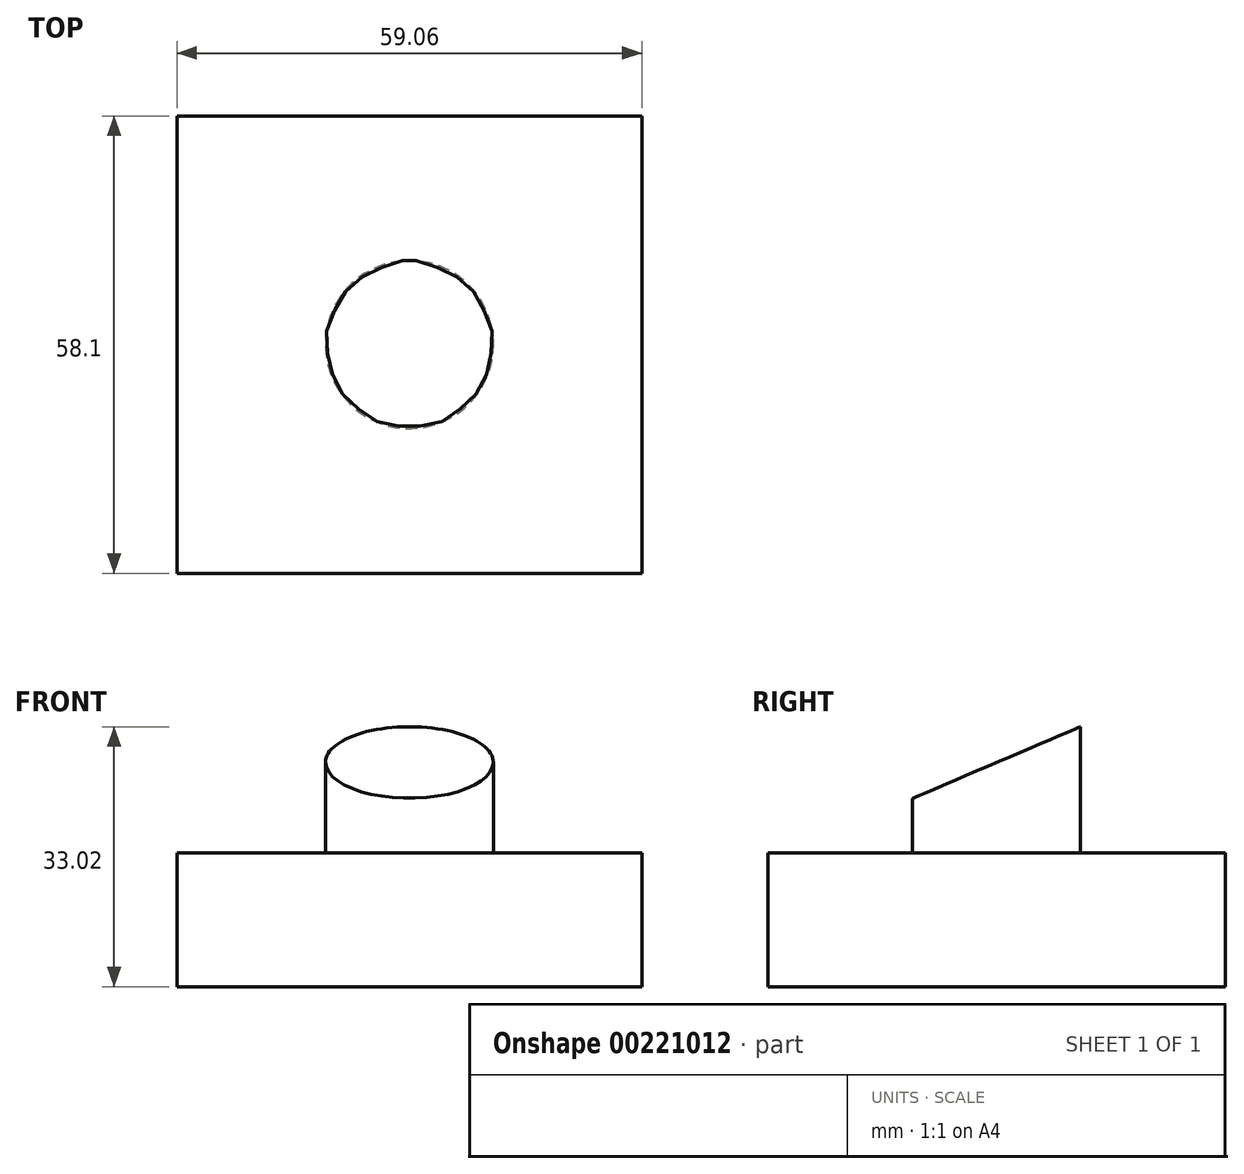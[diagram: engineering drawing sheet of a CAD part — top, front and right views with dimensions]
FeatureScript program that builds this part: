
annotation { "Feature Type Name" : "Feature", "Feature Type Description" : "" }
export const myFeature = defineFeature(function(context is Context, id is Id, definition is map)
    precondition{}
    {
        {
            var Q0;
            Q0=qCreatedBy(makeId("Top.planeOp"),FACE);
            var sketch = newSketch(context, id + "F0", { "sketchPlane" : qUnion([Q0])});
            skLineSegment(sketch, "E0.bottom", {"start": v(-29.53, 29.05) * mm, "end": v(29.53, 29.05) * mm});
            skLineSegment(sketch, "E0.top", {"start": v(-29.53, -29.05) * mm, "end": v(29.53, -29.05) * mm});
            skLineSegment(sketch, "E0.left", {"start": v(-29.53, 29.05) * mm, "end": v(-29.53, -29.05) * mm});
            skLineSegment(sketch, "E0.right", {"start": v(29.53, 29.05) * mm, "end": v(29.53, -29.05) * mm});
            skPoint(sketch, "E0.middle", {"position": v(0, 0) * mm});
            skSolve(sketch);
        }
        {
            var Q0;
            Q0 = qSketchRegion(id + "F0", true);
            extrude(context, id + "F1", {"entities" : qUnion([Q0]), "depth" : 17.02 * mm});
        }
        {
            var Q0;
            Q0=makeQuery(id+"F1.opExtrude","CAP_FACE",FACE,{"disambiguationData":[OSD([sQuery(id+"F0.wireOp",EDGE,"E0.bottom"),sQuery(id+"F0.wireOp",EDGE,"E0.top"),sQuery(id+"F0.wireOp",EDGE,"E0.left"),sQuery(id+"F0.wireOp",EDGE,"E0.right")])],"isStart":false});
            var sketch = newSketch(context, id + "F2", { "sketchPlane" : qUnion([Q0])});
            skCircle(sketch, "E1", {"center": v(0, 0) * mm, "radius": 10.68 * mm});
            skSolve(sketch);
        }
        {
            var Q0;
            Q0 = qSketchRegion(id + "F2", true);
            extrude(context, id + "F3", {"entities" : qUnion([Q0]), "operationType" : NewBodyOperationType.ADD, "depth" : 16 * mm});
        }
        {
            var Q0;
            Q0=qCreatedBy(makeId("Right.planeOp"),FACE);
            var sketch = newSketch(context, id + "F4", { "sketchPlane" : qUnion([Q0])});
            skLineSegment(sketch, "E2", {"start": v(10.68, 33.04) * mm, "end": v(-10.7, 23.9) * mm});
            skLineSegment(sketch, "E3", {"start": v(-10.7, 23.9) * mm, "end": v(-10.7, 33.04) * mm});
            skLineSegment(sketch, "E4", {"start": v(-10.7, 33.04) * mm, "end": v(10.68, 33.04) * mm});
            skSolve(sketch);
        }
        {
            var Q0;
            Q0 = qSketchRegion(id + "F4", true);
            extrude(context, id + "F5", {"entities" : qUnion([Q0]), "operationType" : NewBodyOperationType.REMOVE, "endBound" : BoundingType.THROUGH_ALL, "oppositeDirection" : true, "depth" : 25.4 * mm});
        }
        {
            var Q0;
            Q0=makeQuery(id+"F5.boolean.opBoolean","COPY",FACE,{"derivedFrom":makeQuery(id+"F5.opExtrude","CAP_FACE",FACE,{"disambiguationData":[OSD([sQuery(id+"F4.wireOp",EDGE,"E2"),sQuery(id+"F4.wireOp",EDGE,"E3"),sQuery(id+"F4.wireOp",EDGE,"E4")])],"isStart":true})});
            extrude(context, id + "F6", {"entities" : qUnion([Q0]), "operationType" : NewBodyOperationType.REMOVE, "endBound" : BoundingType.THROUGH_ALL, "oppositeDirection" : true, "depth" : 25.4 * mm});
        }
    });
